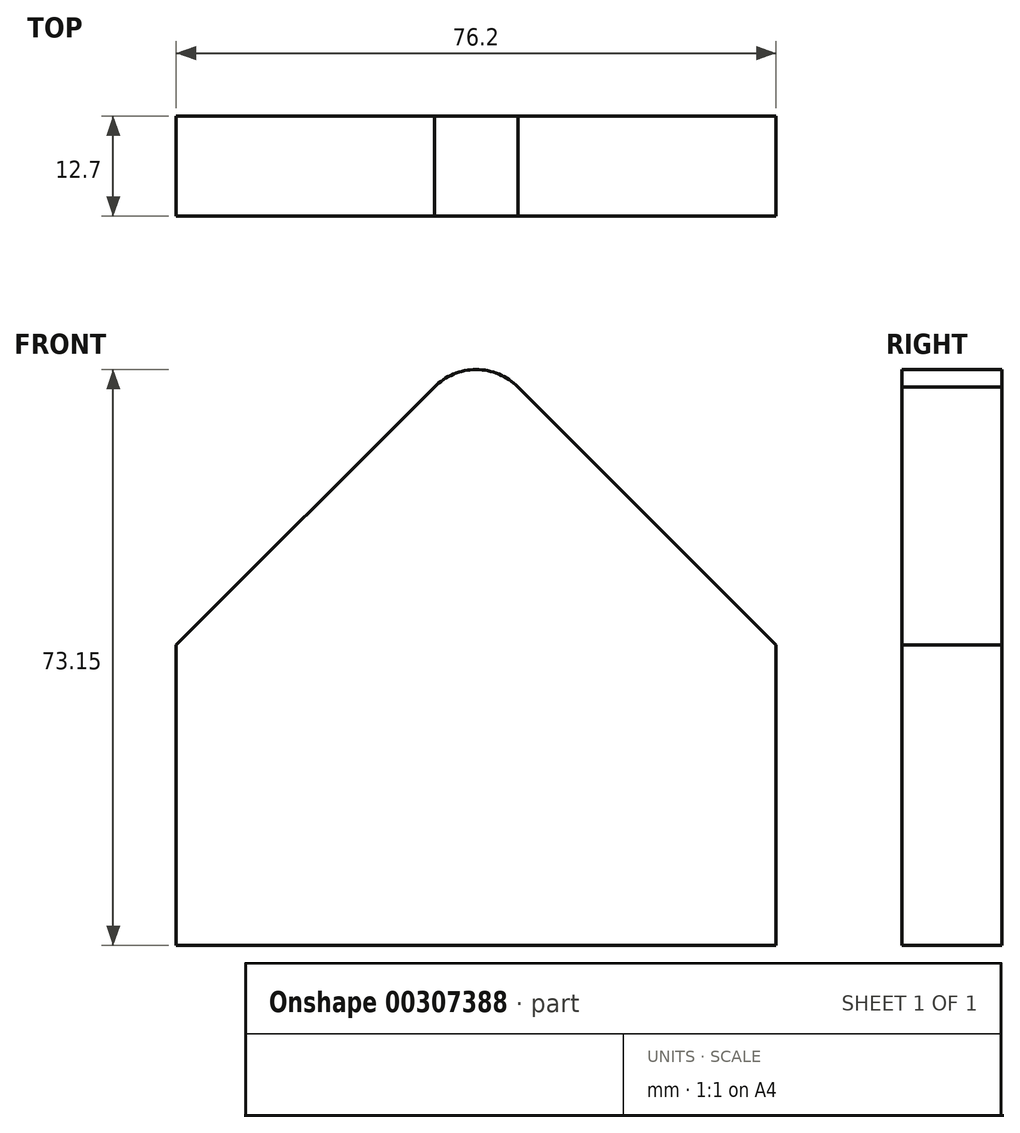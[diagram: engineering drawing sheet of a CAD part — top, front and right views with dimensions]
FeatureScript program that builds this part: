
annotation { "Feature Type Name" : "Feature", "Feature Type Description" : "" }
export const myFeature = defineFeature(function(context is Context, id is Id, definition is map)
    precondition{}
    {
        {
            var Q0;
            Q0=qCreatedBy(makeId("Front.planeOp"),FACE);
            var sketch = newSketch(context, id + "F0", { "sketchPlane" : qUnion([Q0])});
            skLineSegment(sketch, "E0", {"start": v(0, 0) * mm, "end": v(76.2, 0) * mm});
            skLineSegment(sketch, "E1", {"start": v(76.2, 0) * mm, "end": v(76.2, 38.2) * mm});
            skLineSegment(sketch, "E2", {"start": v(76.2, 38.2) * mm, "end": v(43.24, 71.08) * mm});
            skPoint(sketch, "E2.endSnap0", {"position": v(38.1, 0) * mm});
            skLineSegment(sketch, "E3", {"start": v(32.96, 71.08) * mm, "end": v(0, 38.2) * mm});
            skLineSegment(sketch, "E4", {"start": v(0, 38.2) * mm, "end": v(0, 0) * mm});
            skPoint(sketch, "E5.center.orphan", {"position": v(38.1, 65.76) * mm});
            skArc(sketch, "E6", {"start": v(43.4, 70.9) * mm, "mid": v(38.1, 73.15) * mm, "end": v(32.8, 70.9) * mm});
            skPoint(sketch, "E7.orphan", {"position": v(38.1, 76.2) * mm});
            skSolve(sketch);
        }
        {
            var Q0;
            Q0 = qSketchRegion(id + "F0", true);
            extrude(context, id + "F1", {"entities" : qUnion([Q0]), "depth" : 12.7 * mm});
        }
    });
